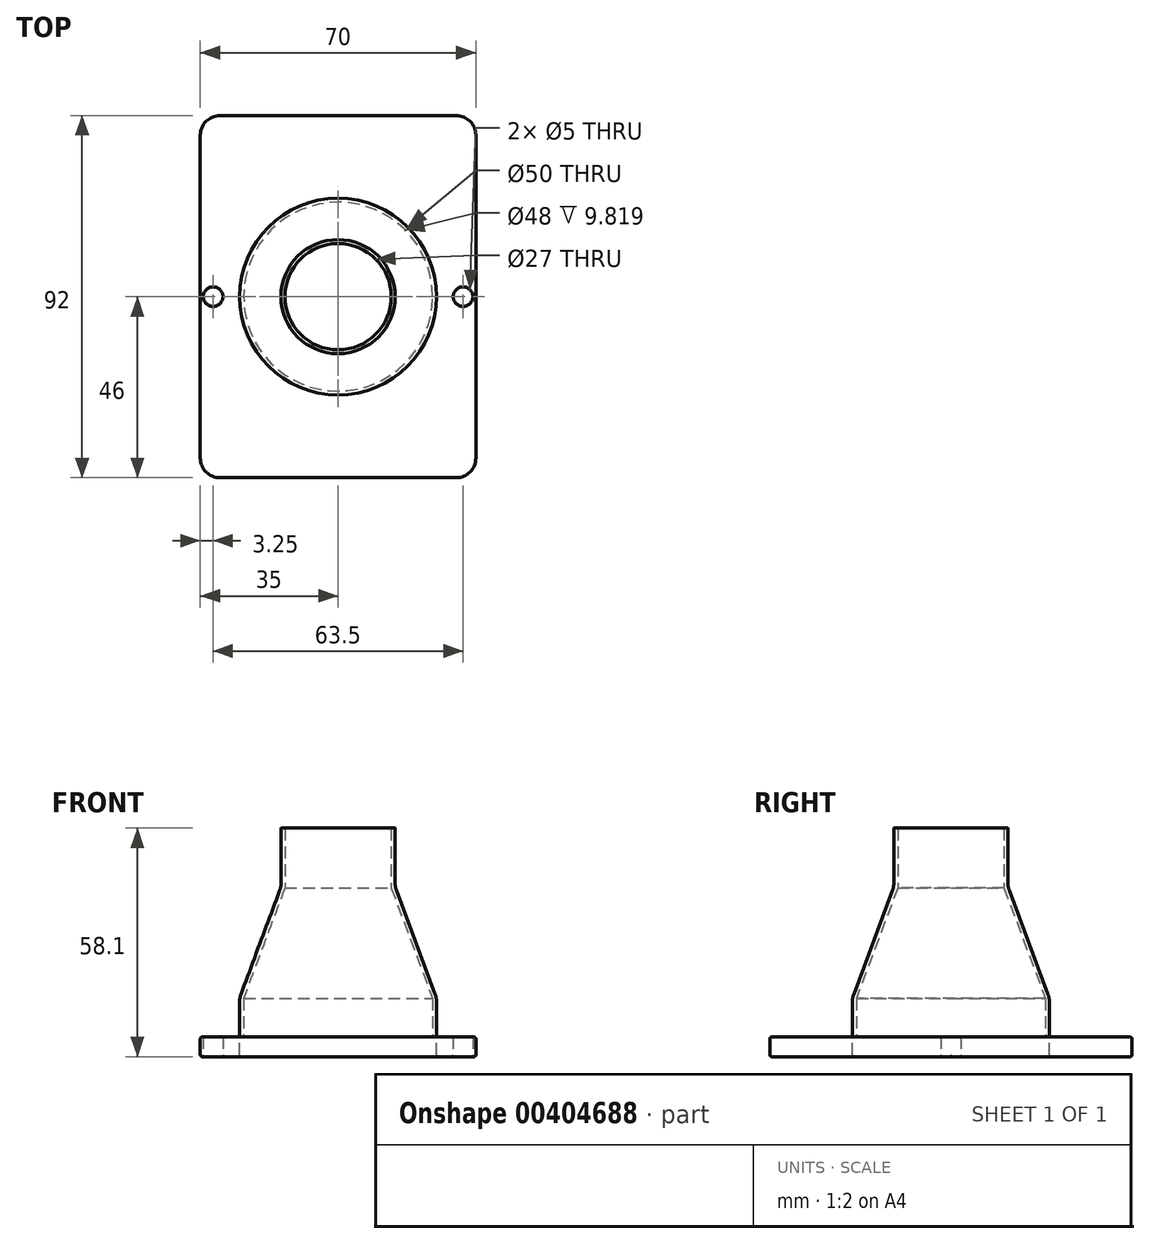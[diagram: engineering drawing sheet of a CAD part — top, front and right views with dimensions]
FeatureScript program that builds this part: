
annotation { "Feature Type Name" : "Feature", "Feature Type Description" : "" }
export const myFeature = defineFeature(function(context is Context, id is Id, definition is map)
    precondition{}
    {
        {
            var Q0;
            Q0=qCreatedBy(makeId("Front.planeOp"),FACE);
            var sketch = newSketch(context, id + "F0", { "sketchPlane" : qUnion([Q0])});
            skLineSegment(sketch, "E0", {"start": v(-25, 0) * mm, "end": v(-25, 10) * mm});
            skLineSegment(sketch, "E1", {"start": v(-25, 10) * mm, "end": v(-14.5, 38.1) * mm});
            skLineSegment(sketch, "E2", {"start": v(-14.5, 38.1) * mm, "end": v(-14.5, 53.1) * mm});
            skLineSegment(sketch, "E3.0", {"start": v(-13.5, 37.92) * mm, "end": v(-13.5, 53.1) * mm});
            skLineSegment(sketch, "E3.1", {"start": v(-24, 9.82) * mm, "end": v(-13.5, 37.92) * mm});
            skLineSegment(sketch, "E3.2", {"start": v(-24, 0) * mm, "end": v(-24, 9.82) * mm});
            skLineSegment(sketch, "E4", {"start": v(-25, 0) * mm, "end": v(-24, 0) * mm});
            skLineSegment(sketch, "E5", {"start": v(-14.5, 53.1) * mm, "end": v(-13.5, 53.1) * mm});
            skLineSegment(sketch, "E6", {"start": v(0, 0) * mm, "end": v(0, 46.9) * mm, "construction": true});
            skSolve(sketch);
        }
        {
            var Q0;
            Q0=makeQuery(id+"F0.imprint","IMPRINT",FACE,{"disambiguationData":[TD([[makeQuery(id+"F0.imprint","IMPRINT",EDGE,{"derivedFrom":sQuery(id+"F0.wireOp",EDGE,"E0")}),-1.0]])]});
            var Q1;
            Q1=sQuery(id+"F0.wireOp",EDGE,"E6");
            revolve(context, id + "F1", {"entities" : qUnion([Q0]), "axis" : qUnion([Q1]), "revolveType" : RevolveType.FULL});
        }
        {
            var Q0;
            Q0=makeQuery(id+"F1.opRevolve","SWEPT_FACE",FACE,{"disambiguationData":[OSD([sQuery(id+"F0.wireOp",EDGE,"E4")])]});
            var sketch = newSketch(context, id + "F2", { "sketchPlane" : qUnion([Q0])});
            skLineSegment(sketch, "E7.bottom", {"start": v(35, 46) * mm, "end": v(-35, 46) * mm});
            skLineSegment(sketch, "E7.top", {"start": v(35, -46) * mm, "end": v(-35, -46) * mm});
            skLineSegment(sketch, "E7.left", {"start": v(35, 46) * mm, "end": v(35, -46) * mm});
            skLineSegment(sketch, "E7.right", {"start": v(-35, 46) * mm, "end": v(-35, -46) * mm});
            skPoint(sketch, "E7.middle", {"position": v(0, 0) * mm});
            skCircle(sketch, "E8", {"center": v(0, 0) * mm, "radius": 25 * mm});
            skSolve(sketch);
        }
        {
            var Q0;
            Q0 = qSketchRegion(id + "F2", true);
            var Q1;
            Q1=makeQuery(id+"F2.imprint","IMPRINT",FACE,{"disambiguationData":[TD([[makeQuery(id+"F2.imprint","IMPRINT",EDGE,{"derivedFrom":sQuery(id+"F2.wireOp",EDGE,"E7.bottom")}),1.0]])]});
            extrude(context, id + "F3", {"entities" : qUnion([Q0, Q1]), "depth" : 5 * mm});
        }
        {
            var Q0;
            Q0=makeQuery(id+"F3.opExtrude","CAP_FACE",FACE,{"disambiguationData":[OSD([sQuery(id+"F2.wireOp",EDGE,"E7.bottom"),sQuery(id+"F2.wireOp",EDGE,"E7.top"),sQuery(id+"F2.wireOp",EDGE,"E7.left"),sQuery(id+"F2.wireOp",EDGE,"E7.right"),sQuery(id+"F2.wireOp",EDGE,"E8")])],"isStart":false});
            var sketch = newSketch(context, id + "F4", { "sketchPlane" : qUnion([Q0])});
            skLineSegment(sketch, "E9", {"start": v(0, 0) * mm, "end": v(0, 35.78) * mm, "construction": true});
            skLineSegment(sketch, "E10", {"start": v(0, 35.78) * mm, "end": v(-0.85, 35.78) * mm, "construction": true});
            skLineSegment(sketch, "E11", {"start": v(0, 0) * mm, "end": v(0, -41.13) * mm, "construction": true});
            skLineSegment(sketch, "E12", {"start": v(0, 0) * mm, "end": v(47.63, 0) * mm, "construction": true});
            skPoint(sketch, "E12.endSnap0", {"position": v(35, 0) * mm});
            skLineSegment(sketch, "E13", {"start": v(47.63, 0) * mm, "end": v(47.63, 0.79) * mm, "construction": true});
            skLineSegment(sketch, "E14", {"start": v(0, 0) * mm, "end": v(-49.33, 0) * mm, "construction": true});
            skLineSegment(sketch, "E15.0", {"start": v(31.75, 0) * mm, "end": v(31.75, 35.78) * mm, "construction": true});
            skLineSegment(sketch, "E16.0", {"start": v(-31.75, 0) * mm, "end": v(-31.75, 35.78) * mm, "construction": true});
            skCircle(sketch, "E17", {"center": v(-31.75, 0) * mm, "radius": 2.5 * mm});
            skCircle(sketch, "E18", {"center": v(31.75, 0) * mm, "radius": 2.5 * mm});
            skSolve(sketch);
        }
        {
            var Q0;
            Q0 = qSketchRegion(id + "F4", true);
            extrude(context, id + "F5", {"entities" : qUnion([Q0]), "operationType" : NewBodyOperationType.REMOVE, "oppositeDirection" : true, "depth" : 25 * mm});
        }
        {
            var Q0;
            Q0=makeQuery(id+"F3.opExtrude","CAP_FACE",FACE,{"disambiguationData":[OSD([sQuery(id+"F2.wireOp",EDGE,"E7.bottom"),sQuery(id+"F2.wireOp",EDGE,"E7.top"),sQuery(id+"F2.wireOp",EDGE,"E7.left"),sQuery(id+"F2.wireOp",EDGE,"E7.right"),sQuery(id+"F2.wireOp",EDGE,"E8")])],"isStart":false});
            fillet(context, id + "F6", {"entities" : qUnion([Q0]), "radius" : .5 * mm, "tangentPropagation" : true, "allowEdgeOverflow" : false});
        }
        {
            var Q0;
            Q0=makeQuery(id+"F3.opExtrude","SWEPT_EDGE",EDGE,{"disambiguationData":[OSD([sQuery(id+"F2.wireOp",EDGE,"E7.bottom"),sQuery(id+"F2.wireOp",EDGE,"E7.left")])]});
            var Q1;
            Q1=makeQuery(id+"F3.opExtrude","SWEPT_EDGE",EDGE,{"disambiguationData":[OSD([sQuery(id+"F2.wireOp",EDGE,"E7.top"),sQuery(id+"F2.wireOp",EDGE,"E7.left")])]});
            var Q2;
            Q2=makeQuery(id+"F3.opExtrude","SWEPT_EDGE",EDGE,{"disambiguationData":[OSD([sQuery(id+"F2.wireOp",EDGE,"E7.bottom"),sQuery(id+"F2.wireOp",EDGE,"E7.right")])]});
            var Q3;
            Q3=makeQuery(id+"F3.opExtrude","SWEPT_EDGE",EDGE,{"disambiguationData":[OSD([sQuery(id+"F2.wireOp",EDGE,"E7.top"),sQuery(id+"F2.wireOp",EDGE,"E7.right")])]});
            fillet(context, id + "F7", {"entities" : qUnion([Q0, Q1, Q2, Q3]), "radius" : 5 * mm, "tangentPropagation" : true, "allowEdgeOverflow" : false});
        }
        {
            var Q0;
            Q0=makeQuery(id+"F3.opExtrude","CAP_EDGE",EDGE,{"disambiguationData":[OSD([sQuery(id+"F2.wireOp",EDGE,"E7.bottom")])],"isStart":true});
            fillet(context, id + "F8", {"entities" : qUnion([Q0]), "radius" : .5 * mm, "tangentPropagation" : true, "allowEdgeOverflow" : false});
        }
        {
            var Q0;
            Q0=makeQuery(id+"F1.opRevolve","SWEPT_EDGE",EDGE,{"disambiguationData":[OSD([sQuery(id+"F0.wireOp",EDGE,"E0"),sQuery(id+"F0.wireOp",EDGE,"E1")])]});
            var Q1;
            {var subQ0=sQuery(id+"F2.wireOp",EDGE,"E8");Q1=makeQuery(id+"F8.opFillet","BLEND_EDGE",EDGE,{"blendedFrom":[makeQuery(id+"F3.opExtrude","CAP_EDGE",EDGE,{"disambiguationData":[OSD([subQ0])],"isStart":true}),makeQuery(id+"F3.opExtrude","CAP_FACE",FACE,{"disambiguationData":[OSD([sQuery(id+"F2.wireOp",EDGE,"E7.bottom"),sQuery(id+"F2.wireOp",EDGE,"E7.top"),sQuery(id+"F2.wireOp",EDGE,"E7.left"),sQuery(id+"F2.wireOp",EDGE,"E7.right"),subQ0])],"isStart":true})],"blendedInto":[makeQuery(id+"F3.opExtrude","CAP_FACE",FACE,{"disambiguationData":[OSD([sQuery(id+"F2.wireOp",EDGE,"E7.bottom"),sQuery(id+"F2.wireOp",EDGE,"E7.top"),sQuery(id+"F2.wireOp",EDGE,"E7.left"),sQuery(id+"F2.wireOp",EDGE,"E7.right"),subQ0])],"isStart":true})]});}
            var Q2;
            Q2=makeQuery(id+"F1.opRevolve","SWEPT_EDGE",EDGE,{"disambiguationData":[OSD([sQuery(id+"F0.wireOp",EDGE,"E1"),sQuery(id+"F0.wireOp",EDGE,"E2")])]});
            fillet(context, id + "F9", {"entities" : qUnion([Q0, Q1, Q2]), "radius" : 5 * mm, "tangentPropagation" : true, "allowEdgeOverflow" : false});
        }
        {
            var Q0;
            Q0=makeQuery(id+"F1.opRevolve","SWEPT_FACE",FACE,{"disambiguationData":[OSD([sQuery(id+"F0.wireOp",EDGE,"E5")])]});
            fillet(context, id + "F10", {"entities" : qUnion([Q0]), "radius" : .1 * mm, "tangentPropagation" : true, "allowEdgeOverflow" : false});
        }
    });
